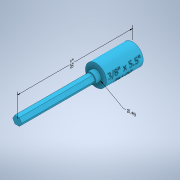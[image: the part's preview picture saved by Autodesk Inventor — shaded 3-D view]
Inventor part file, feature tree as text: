
AUTODESK INVENTOR PART (.ipt)
format: ipt  version: 2022.2 (Build 262287030, 287C)  size: 642,048 bytes
history: native  units: in
note: dims shown in document units (in); Inventor stores cm internally (conversion verified against a paired STEP export)
features: sketch x6, other x5, extrude x5, plane x1, emboss x1
ambient origin geometry x8: Origin, YZ Plane, XZ Plane, XY Plane, X Axis, Y Axis, Z Axis, Center Point
bodies: Body1 (feature_tree)
feature tree (18):
  other  "Annotations"
  extrude  "Extrusion2"  Depth=4.5in TaperAngle=0.0deg
  extrude  "Extrusion4"  Depth=1.0in
  other  "Reduce Hex Shaft"
  extrude  "Extrusion5"  Depth=0.005in
  other  "Reduce Base Bushing"
  extrude  "Extrusion7"  Depth=0.5in
  plane  "Work Plane1"
  emboss  "Emboss3"
  extrude  "Extrusion8"  Depth=0.25in
  sketch  "Sketch1"  dims[d0=0.375in d4=4.5in d5=0.0in]
  sketch  "Sketch4"  dims[d6=0.001in d10=1.0in]
  sketch  "Sketch5"  dims[d11=0.75in d12=0.0in d13=0.005in]
  sketch  "Sketch8"  dims[d14=0.005in d15=0.5in]
  sketch  "Sketch10"  dims[d16=0.25in d17=0.0in d20=0.005in]
  sketch  "Sketch11"  dims[d21=0.005in d29=1.0in d30=0.0in d37=0.1in d38=0.0in d39=0.52in d40=1.5in d41=0.0in d23=2.2764in d24=0.49in d31=5.5in]
  other  "Diameter Dimension 1"
  other  "Linear Dimension 1"
